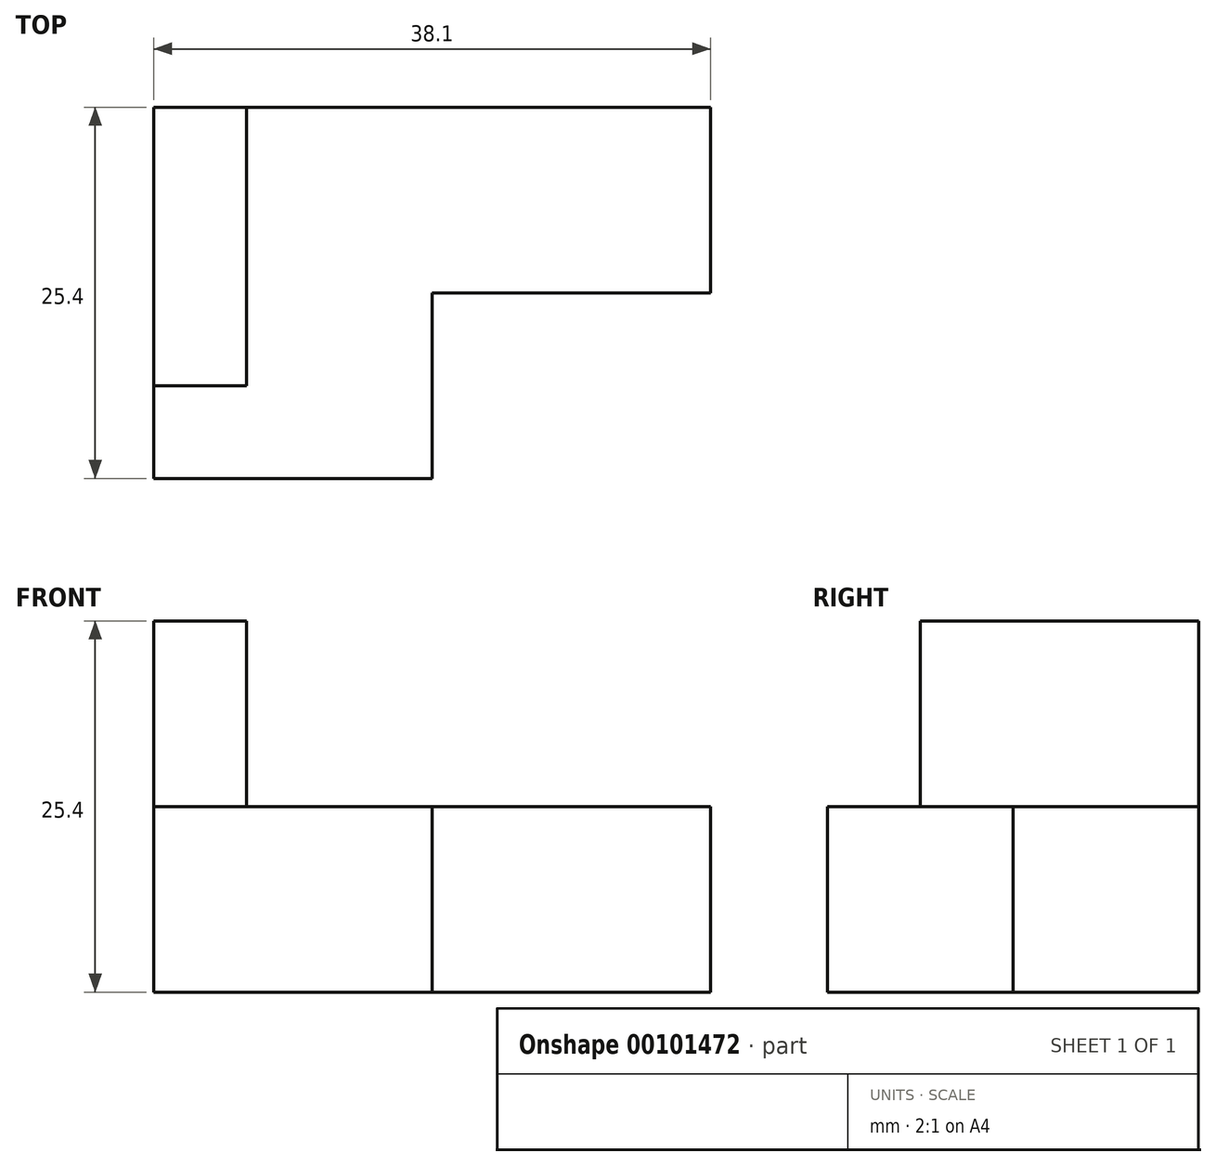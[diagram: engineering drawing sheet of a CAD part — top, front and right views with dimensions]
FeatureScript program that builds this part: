
annotation { "Feature Type Name" : "Feature", "Feature Type Description" : "" }
export const myFeature = defineFeature(function(context is Context, id is Id, definition is map)
    precondition{}
    {
        {
            var Q0;
            Q0=qCreatedBy(makeId("Top.planeOp"),FACE);
            var sketch = newSketch(context, id + "F0", { "sketchPlane" : qUnion([Q0])});
            skLineSegment(sketch, "E0", {"start": v(0, 0) * mm, "end": v(19.05, 0) * mm});
            skLineSegment(sketch, "E1", {"start": v(19.05, 0) * mm, "end": v(19.05, 12.7) * mm});
            skLineSegment(sketch, "E2", {"start": v(19.05, 12.7) * mm, "end": v(38.1, 12.7) * mm});
            skLineSegment(sketch, "E3", {"start": v(38.1, 12.7) * mm, "end": v(38.1, 25.4) * mm});
            skLineSegment(sketch, "E4", {"start": v(6.35, 25.4) * mm, "end": v(6.35, 6.35) * mm});
            skLineSegment(sketch, "E5", {"start": v(6.35, 6.35) * mm, "end": v(0, 6.35) * mm});
            skLineSegment(sketch, "E6", {"start": v(6.35, 25.4) * mm, "end": v(38.1, 25.4) * mm});
            skLineSegment(sketch, "E7", {"start": v(0, 6.35) * mm, "end": v(0, 0) * mm});
            skLineSegment(sketch, "E8", {"start": v(0, 6.35) * mm, "end": v(0, 25.4) * mm});
            skLineSegment(sketch, "E9", {"start": v(0, 25.4) * mm, "end": v(6.35, 25.4) * mm});
            skSolve(sketch);
        }
        {
            var Q0;
            Q0=makeQuery(id+"F0.imprint","IMPRINT",FACE,{"disambiguationData":[TD([[makeQuery(id+"F0.imprint","IMPRINT",EDGE,{"derivedFrom":sQuery(id+"F0.wireOp",EDGE,"E4")}),-1.0]])]});
            var Q1;
            Q1=makeQuery(id+"F0.imprint","IMPRINT",FACE,{"disambiguationData":[TD([[makeQuery(id+"F0.imprint","IMPRINT",EDGE,{"derivedFrom":sQuery(id+"F0.wireOp",EDGE,"E0")}),1.0]])]});
            extrude(context, id + "F1", {"entities" : qUnion([Q0, Q1]), "depth" : 12.7 * mm});
        }
        {
            var Q0;
            Q0=qCreatedBy(makeId("Right.planeOp"),FACE);
            var sketch = newSketch(context, id + "F2", { "sketchPlane" : qUnion([Q0])});
            skLineSegment(sketch, "E10", {"start": v(25.4, 0) * mm, "end": v(25.4, 25.4) * mm});
            skLineSegment(sketch, "E11", {"start": v(25.4, 25.4) * mm, "end": v(6.35, 25.4) * mm});
            skLineSegment(sketch, "E12", {"start": v(6.35, 25.4) * mm, "end": v(6.35, 0) * mm});
            skLineSegment(sketch, "E13", {"start": v(6.35, 0) * mm, "end": v(25.4, 0) * mm});
            skSolve(sketch);
        }
        {
            var Q0;
            Q0 = qSketchRegion(id + "F2", true);
            extrude(context, id + "F3", {"entities" : qUnion([Q0]), "operationType" : NewBodyOperationType.ADD, "depth" : 6.35 * mm});
        }
    });
